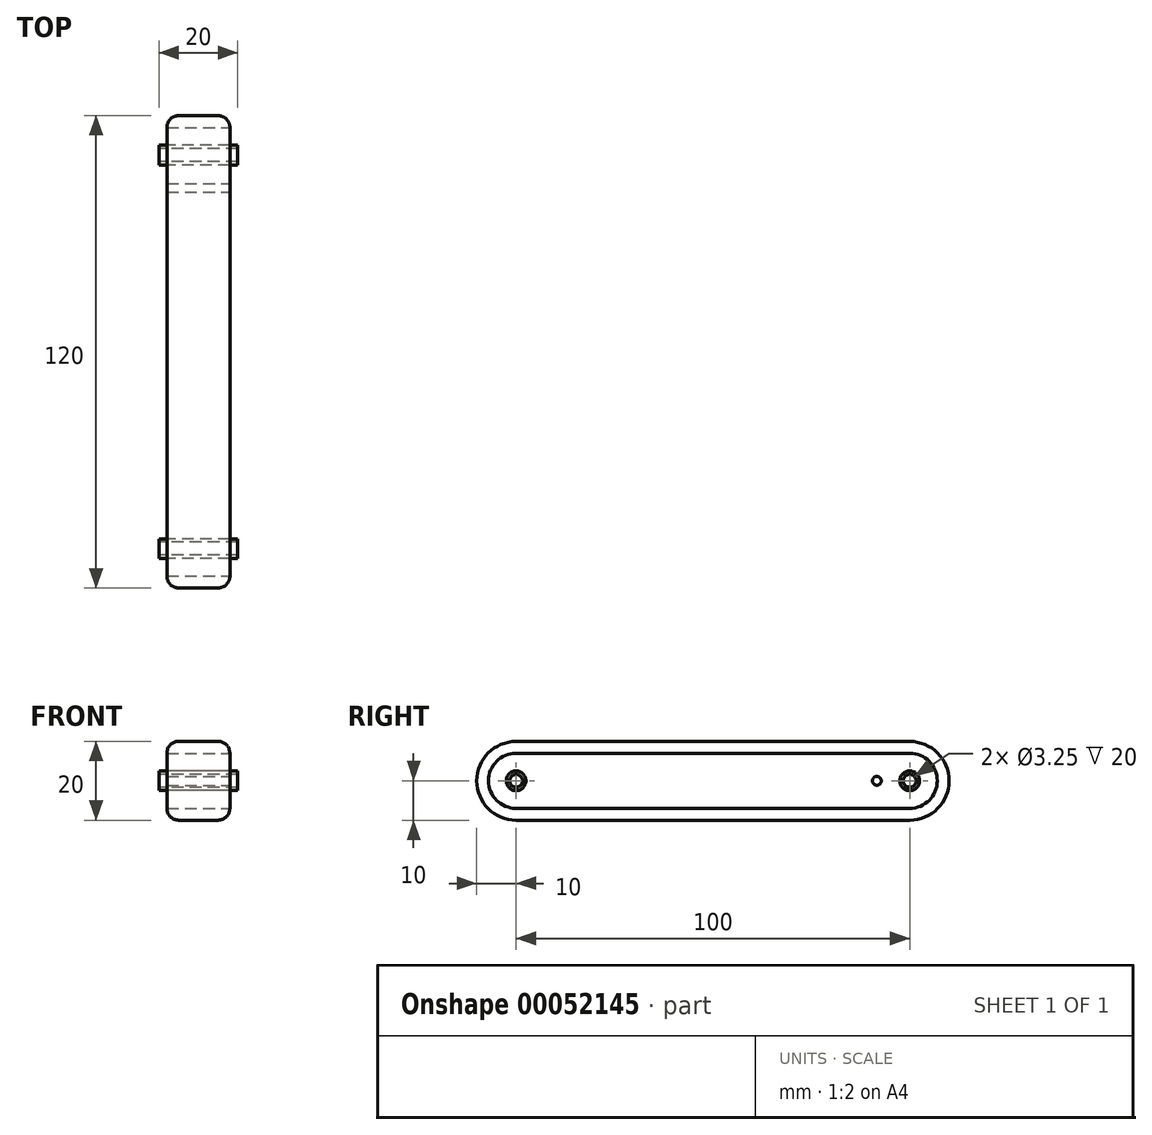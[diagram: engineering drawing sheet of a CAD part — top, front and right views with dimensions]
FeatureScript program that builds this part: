
annotation { "Feature Type Name" : "Feature", "Feature Type Description" : "" }
export const myFeature = defineFeature(function(context is Context, id is Id, definition is map)
    precondition{}
    {
        {
            var Q0;
            Q0=qCreatedBy(makeId("Right.planeOp"),FACE);
            var sketch = newSketch(context, id + "F0", { "sketchPlane" : qUnion([Q0])});
            skLineSegment(sketch, "E0.bottom", {"start": v(0, 10) * mm, "end": v(-50, 10) * mm});
            skLineSegment(sketch, "E0.top", {"start": v(0, -10) * mm, "end": v(-50, -10) * mm});
            skLineSegment(sketch, "E0.left", {"start": v(0, 10) * mm, "end": v(0, -10) * mm});
            skArc(sketch, "E1", {"start": v(-50, 10) * mm, "mid": v(-60, 0) * mm, "end": v(-50, -10) * mm});
            skCircle(sketch, "E2", {"center": v(-50, 0) * mm, "radius": 1.63 * mm});
            skSolve(sketch);
        }
        {
            var Q0;
            Q0=makeQuery(id+"F0.imprint","IMPRINT",FACE,{"disambiguationData":[TD([[makeQuery(id+"F0.imprint","IMPRINT",EDGE,{"derivedFrom":sQuery(id+"F0.wireOp",EDGE,"E0.bottom")}),1.0]])]});
            extrude(context, id + "F1", {"entities" : qUnion([Q0]), "depth" : 8 * mm});
        }
        {
            var Q0;
            Q0=makeQuery(id+"F1.opExtrude","CAP_FACE",FACE,{"disambiguationData":[OSD([sQuery(id+"F0.wireOp",EDGE,"E0.bottom"),sQuery(id+"F0.wireOp",EDGE,"E0.top"),sQuery(id+"F0.wireOp",EDGE,"E0.left"),sQuery(id+"F0.wireOp",EDGE,"E1"),sQuery(id+"F0.wireOp",EDGE,"E2")])],"isStart":false});
            var sketch = newSketch(context, id + "F2", { "sketchPlane" : qUnion([Q0])});
            skCircle(sketch, "E3", {"center": v(-50, 0) * mm, "radius": 1.63 * mm});
            skCircle(sketch, "E4", {"center": v(-50, 0) * mm, "radius": 2.5 * mm});
            skSolve(sketch);
        }
        {
            var Q0;
            Q0=makeQuery(id+"F2.imprint","IMPRINT",FACE,{"disambiguationData":[TD([[makeQuery(id+"F2.imprint","IMPRINT",EDGE,{"derivedFrom":sQuery(id+"F2.wireOp",EDGE,"E3")}),-1.0]])]});
            extrude(context, id + "F3", {"entities" : qUnion([Q0]), "operationType" : NewBodyOperationType.ADD, "depth" : 2 * mm});
        }
        {
            var Q0;
            Q0=makeQuery(id+"F1.opExtrude","CAP_EDGE",EDGE,{"disambiguationData":[OSD([sQuery(id+"F0.wireOp",EDGE,"E0.bottom")])],"isStart":false});
            fillet(context, id + "F4", {"entities" : qUnion([Q0]), "radius" : 3 * mm, "tangentPropagation" : true, "allowEdgeOverflow" : false});
        }
        {
            var Q0;
            Q0=makeQuery(id+"F1.opExtrude","SWEPT_BODY",BODY,{"disambiguationData":[OSD([sQuery(id+"F0.wireOp",EDGE,"E0.bottom"),sQuery(id+"F0.wireOp",EDGE,"E0.top"),sQuery(id+"F0.wireOp",EDGE,"E0.left"),sQuery(id+"F0.wireOp",EDGE,"E1"),sQuery(id+"F0.wireOp",EDGE,"E2")])]});
            var Q1;
            Q1=qCreatedBy(makeId("Right.planeOp"),FACE);
            mirror(context, id + "F5", {"operationType" : NewBodyOperationType.ADD, "entities" : qUnion([Q0]), "mirrorPlane" : qUnion([Q1])});
        }
        {
            var Q0;
            Q0=makeQuery(id+"F1.opExtrude","SWEPT_BODY",BODY,{"disambiguationData":[OSD([sQuery(id+"F0.wireOp",EDGE,"E0.bottom"),sQuery(id+"F0.wireOp",EDGE,"E0.top"),sQuery(id+"F0.wireOp",EDGE,"E0.left"),sQuery(id+"F0.wireOp",EDGE,"E1"),sQuery(id+"F0.wireOp",EDGE,"E2")])]});
            var Q1;
            Q1=qCreatedBy(makeId("Front.planeOp"),FACE);
            mirror(context, id + "F6", {"operationType" : NewBodyOperationType.ADD, "entities" : qUnion([Q0]), "mirrorPlane" : qUnion([Q1])});
        }
        {
            var Q0;
            {var subQ0=makeQuery(id+"F1.opExtrude","CAP_FACE",FACE,{"disambiguationData":[OSD([sQuery(id+"F0.wireOp",EDGE,"E0.bottom"),sQuery(id+"F0.wireOp",EDGE,"E0.top"),sQuery(id+"F0.wireOp",EDGE,"E0.left"),sQuery(id+"F0.wireOp",EDGE,"E1"),sQuery(id+"F0.wireOp",EDGE,"E2")])],"isStart":false});Q0=makeQuery(id+"F6.boolean.opBoolean","MERGE",FACE,{"derivedFrom":[subQ0,makeQuery(id+"F6.opPattern","COPY",FACE,{"derivedFrom":subQ0,"instanceName":"1"})]});}
            var sketch = newSketch(context, id + "F7", { "sketchPlane" : qUnion([Q0])});
            skLineSegment(sketch, "E5.rect.bottom", {"start": v(38.66, -6.5) * mm, "end": v(15.66, -6.5) * mm});
            skLineSegment(sketch, "E5.rect.top", {"start": v(38.66, 6.5) * mm, "end": v(15.66, 6.5) * mm});
            skLineSegment(sketch, "E5.rect.left", {"start": v(38.66, -6.5) * mm, "end": v(38.66, -2.5) * mm});
            skLineSegment(sketch, "E5.rect.right", {"start": v(15.66, -6.5) * mm, "end": v(15.66, -2.5) * mm});
            skPoint(sketch, "E5.rect.middle", {"position": v(27.16, 0) * mm});
            skLineSegment(sketch, "E6", {"start": v(27.16, 0) * mm, "end": v(27.16, -12.66) * mm, "construction": true});
            skPoint(sketch, "E6.endSnap0", {"position": v(27.16, -6.5) * mm});
            skLineSegment(sketch, "E7.rect.bottom", {"start": v(15.66, -2.5) * mm, "end": v(14.16, -2.5) * mm});
            skLineSegment(sketch, "E7.rect.top", {"start": v(15.66, 2.5) * mm, "end": v(14.16, 2.5) * mm});
            skLineSegment(sketch, "E7.rect.right", {"start": v(14.16, -2.5) * mm, "end": v(14.16, 2.5) * mm});
            skPoint(sketch, "E7.rect.middle", {"position": v(14.9, 0) * mm});
            skLineSegment(sketch, "E8.trimOffspring", {"start": v(15.66, 2.5) * mm, "end": v(15.66, 6.5) * mm});
            skCircle(sketch, "E9", {"center": v(12.66, 0) * mm, "radius": 1.13 * mm});
            skLineSegment(sketch, "E10.MirrorCS", {"start": v(4.16, 0) * mm, "end": v(4.16, -12.66) * mm, "construction": true});
            skLineSegment(sketch, "E11.MirrorCS", {"start": v(38.66, 2.5) * mm, "end": v(40.16, 2.5) * mm});
            skLineSegment(sketch, "E12.MirrorCS", {"start": v(40.16, -2.5) * mm, "end": v(40.16, 2.5) * mm});
            skLineSegment(sketch, "E13.MirrorCS", {"start": v(38.66, -2.5) * mm, "end": v(40.16, -2.5) * mm});
            skCircle(sketch, "E14.MirrorC", {"center": v(41.66, 0) * mm, "radius": 1.13 * mm});
            skLineSegment(sketch, "E15.trimOffspring", {"start": v(38.66, 2.5) * mm, "end": v(38.66, 6.5) * mm});
            skSolve(sketch);
        }
        {
            var Q0;
            Q0=makeQuery(id+"F7.imprint","IMPRINT",FACE,{"disambiguationData":[TD([[makeQuery(id+"F7.imprint","IMPRINT",EDGE,{"derivedFrom":sQuery(id+"F7.wireOp",EDGE,"E5.rect.bottom")}),-1.0]])]});
            var Q1;
            Q1=makeQuery(id+"F7.imprint","IMPRINT",FACE,{"disambiguationData":[TD([[makeQuery(id+"F7.imprint","IMPRINT",EDGE,{"derivedFrom":sQuery(id+"F7.wireOp",EDGE,"E9")}),1.0]])]});
            var Q2;
            Q2=makeQuery(id+"F7.imprint","IMPRINT",FACE,{"disambiguationData":[TD([[makeQuery(id+"F7.imprint","IMPRINT",EDGE,{"derivedFrom":sQuery(id+"F7.wireOp",EDGE,"E14.MirrorC")}),-1.0]])]});
            var Q3;
            {var subQ0=makeQuery(id+"F5.opPattern","COPY",FACE,{"derivedFrom":makeQuery(id+"F1.opExtrude","CAP_FACE",FACE,{"disambiguationData":[OSD([sQuery(id+"F0.wireOp",EDGE,"E0.bottom"),sQuery(id+"F0.wireOp",EDGE,"E0.top"),sQuery(id+"F0.wireOp",EDGE,"E0.left"),sQuery(id+"F0.wireOp",EDGE,"E1"),sQuery(id+"F0.wireOp",EDGE,"E2")])],"isStart":false}),"instanceName":"1"});Q3=makeQuery(id+"F6.boolean.opBoolean","MERGE",FACE,{"derivedFrom":[subQ0,makeQuery(id+"F6.opPattern","COPY",FACE,{"derivedFrom":subQ0,"instanceName":"1"})]});}
            extrude(context, id + "F8", {"entities" : qUnion([Q0, Q1, Q2]), "operationType" : NewBodyOperationType.REMOVE, "endBound" : BoundingType.UP_TO_SURFACE, "oppositeDirection" : true, "endBoundEntityFace" : qUnion([Q3]), "depth" : 25 * mm});
        }
        {
            var Q0;
            {var subQ0=makeQuery(id+"F1.opExtrude","CAP_FACE",FACE,{"disambiguationData":[OSD([sQuery(id+"F0.wireOp",EDGE,"E0.bottom"),sQuery(id+"F0.wireOp",EDGE,"E0.top"),sQuery(id+"F0.wireOp",EDGE,"E0.left"),sQuery(id+"F0.wireOp",EDGE,"E1"),sQuery(id+"F0.wireOp",EDGE,"E2")])],"isStart":false});Q0=makeQuery(id+"F6.boolean.opBoolean","MERGE",FACE,{"derivedFrom":[subQ0,makeQuery(id+"F6.opPattern","COPY",FACE,{"derivedFrom":subQ0,"instanceName":"1"})]});}
            var sketch = newSketch(context, id + "F9", { "sketchPlane" : qUnion([Q0])});
            skLineSegment(sketch, "E16.rect.bottom", {"start": v(10.66, 6.5) * mm, "end": v(43.66, 6.5) * mm});
            skLineSegment(sketch, "E16.rect.top", {"start": v(10.66, -6.5) * mm, "end": v(43.66, -6.5) * mm});
            skLineSegment(sketch, "E16.rect.left", {"start": v(10.66, 6.5) * mm, "end": v(10.66, -6.5) * mm});
            skLineSegment(sketch, "E16.rect.right", {"start": v(43.66, 6.5) * mm, "end": v(43.66, -6.5) * mm});
            skPoint(sketch, "E16.rect.middle", {"position": v(27.16, 0) * mm});
            skLineSegment(sketch, "E17", {"start": v(14.16, 0) * mm, "end": v(27.16, 0) * mm, "construction": true});
            skLineSegment(sketch, "E18", {"start": v(40.16, 0) * mm, "end": v(27.16, 0) * mm, "construction": true});
            skSolve(sketch);
        }
        {
            var Q0;
            {var subQ1=sQuery(id+"F9.wireOp",EDGE,"E16.rect.left");Q0=makeQuery(id+"F9.imprint","IMPRINT",FACE,{"disambiguationData":[TD([[makeQuery(id+"F9.imprint","IMPRINT",EDGE,{"derivedFrom":subQ1}),1.0]])]});}
            var Q1;
            {var subQ2=sQuery(id+"F9.wireOp",EDGE,"E16.rect.right");Q1=makeQuery(id+"F9.imprint","IMPRINT",FACE,{"disambiguationData":[TD([[makeQuery(id+"F9.imprint","IMPRINT",EDGE,{"derivedFrom":subQ2}),-1.0]])]});}
            extrude(context, id + "F10", {"entities" : qUnion([Q0, Q1]), "operationType" : NewBodyOperationType.REMOVE, "oppositeDirection" : true, "depth" : 4.5 * mm});
        }
        {
            var Q0;
            {var subQ0=makeQuery(id+"F5.opPattern","COPY",FACE,{"derivedFrom":makeQuery(id+"F1.opExtrude","CAP_FACE",FACE,{"disambiguationData":[OSD([sQuery(id+"F0.wireOp",EDGE,"E0.bottom"),sQuery(id+"F0.wireOp",EDGE,"E0.top"),sQuery(id+"F0.wireOp",EDGE,"E0.left"),sQuery(id+"F0.wireOp",EDGE,"E1"),sQuery(id+"F0.wireOp",EDGE,"E2")])],"isStart":false}),"instanceName":"1"});Q0=makeQuery(id+"F6.boolean.opBoolean","MERGE",FACE,{"derivedFrom":[subQ0,makeQuery(id+"F6.opPattern","COPY",FACE,{"derivedFrom":subQ0,"instanceName":"1"})]});}
            var sketch = newSketch(context, id + "F11", { "sketchPlane" : qUnion([Q0])});
            skLineSegment(sketch, "E19", {"start": v(-40.16, 0) * mm, "end": v(-27.16, 0) * mm, "construction": true});
            skPoint(sketch, "E19.endSnap0", {"position": v(-40.16, 0) * mm});
            skLineSegment(sketch, "E20", {"start": v(-27.16, 0) * mm, "end": v(-14.16, 0) * mm, "construction": true});
            skLineSegment(sketch, "E21.rect.bottom", {"start": v(-43.66, -6.5) * mm, "end": v(-10.66, -6.5) * mm});
            skLineSegment(sketch, "E21.rect.top", {"start": v(-43.66, 6.5) * mm, "end": v(-10.66, 6.5) * mm});
            skLineSegment(sketch, "E21.rect.left", {"start": v(-43.66, -6.5) * mm, "end": v(-43.66, 6.5) * mm});
            skLineSegment(sketch, "E21.rect.right", {"start": v(-10.66, -6.5) * mm, "end": v(-10.66, 6.5) * mm});
            skPoint(sketch, "E21.rect.middle", {"position": v(-27.16, 0) * mm});
            skSolve(sketch);
        }
        {
            var Q0;
            {var subQ1=sQuery(id+"F11.wireOp",EDGE,"E21.rect.left");Q0=makeQuery(id+"F11.imprint","IMPRINT",FACE,{"disambiguationData":[TD([[makeQuery(id+"F11.imprint","IMPRINT",EDGE,{"derivedFrom":subQ1}),-1.0]])]});}
            var Q1;
            {var subQ3=sQuery(id+"F11.wireOp",EDGE,"E21.rect.right");Q1=makeQuery(id+"F11.imprint","IMPRINT",FACE,{"disambiguationData":[TD([[makeQuery(id+"F11.imprint","IMPRINT",EDGE,{"derivedFrom":subQ3}),1.0]])]});}
            extrude(context, id + "F12", {"entities" : qUnion([Q0, Q1]), "operationType" : NewBodyOperationType.REMOVE, "oppositeDirection" : true, "depth" : 6 * mm});
        }
    });
